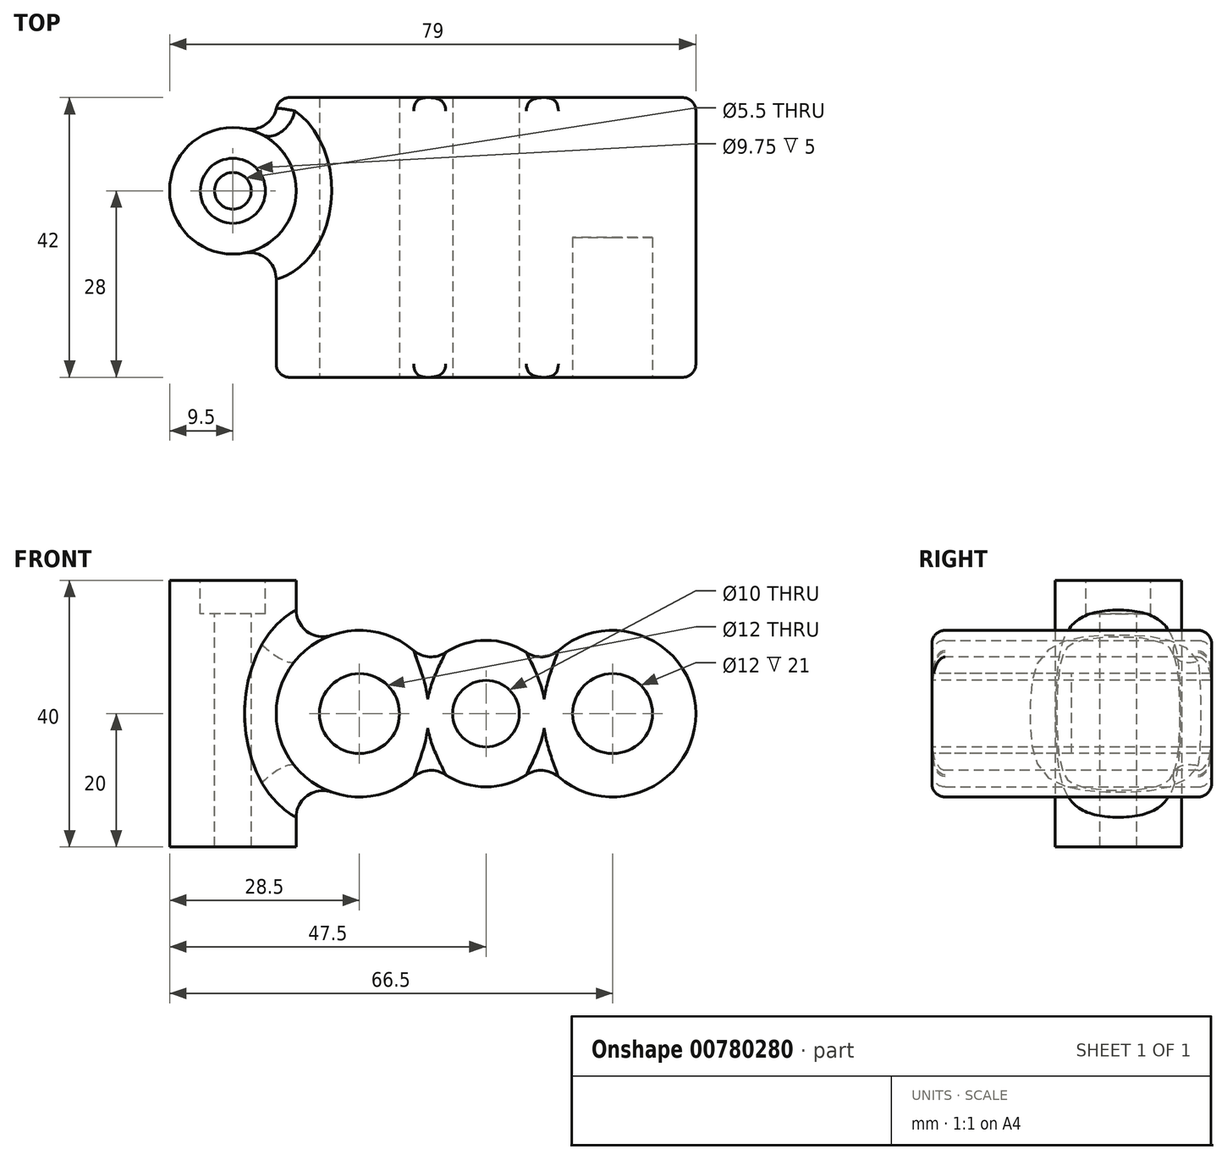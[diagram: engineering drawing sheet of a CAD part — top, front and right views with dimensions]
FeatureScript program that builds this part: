
annotation { "Feature Type Name" : "Feature", "Feature Type Description" : "" }
export const myFeature = defineFeature(function(context is Context, id is Id, definition is map)
    precondition{}
    {
        {
            var Q0;
            Q0=qCreatedBy(makeId("Front.planeOp"),FACE);
            var sketch = newSketch(context, id + "F0", { "sketchPlane" : qUnion([Q0])});
            skArc(sketch, "E0", {"start": v(10.43, 6.9) * mm, "mid": v(-12.5, 0) * mm, "end": v(10.43, -6.9) * mm});
            skArc(sketch, "E1", {"start": v(27.57, 6.9) * mm, "mid": v(19, 11) * mm, "end": v(10.43, 6.9) * mm});
            skArc(sketch, "E2", {"start": v(27.57, -6.9) * mm, "mid": v(50.5, 0) * mm, "end": v(27.57, 6.9) * mm});
            skArc(sketch, "E3.trimOffspring", {"start": v(10.43, -6.9) * mm, "mid": v(19, -11) * mm, "end": v(27.57, -6.9) * mm});
            skSolve(sketch);
        }
        {
            var Q0;
            Q0 = qSketchRegion(id + "F0", true);
            extrude(context, id + "F1", {"entities" : qUnion([Q0]), "depth" : 42 * mm, "offsetDistance" : 25 * mm});
        }
        {
            var Q0;
            Q0=makeQuery(id+"F1.opExtrude","CAP_FACE",FACE,{"disambiguationData":[OSD([sQuery(id+"F0.wireOp",EDGE,"E0"),sQuery(id+"F0.wireOp",EDGE,"E1"),sQuery(id+"F0.wireOp",EDGE,"E2"),sQuery(id+"F0.wireOp",EDGE,"E3.trimOffspring")])],"isStart":false});
            var sketch = newSketch(context, id + "F2", { "sketchPlane" : qUnion([Q0])});
            skCircle(sketch, "E4", {"center": v(0, 0) * mm, "radius": 6 * mm});
            skCircle(sketch, "E5", {"center": v(19, 0) * mm, "radius": 5 * mm});
            skSolve(sketch);
        }
        {
            var Q0;
            Q0 = qSketchRegion(id + "F2", true);
            extrude(context, id + "F3", {"entities" : qUnion([Q0]), "operationType" : NewBodyOperationType.REMOVE, "endBound" : BoundingType.THROUGH_ALL, "oppositeDirection" : true, "depth" : 25 * mm, "offsetDistance" : 25 * mm});
        }
        {
            var Q0;
            Q0=makeQuery(id+"F1.opExtrude","CAP_FACE",FACE,{"disambiguationData":[OSD([sQuery(id+"F0.wireOp",EDGE,"E0"),sQuery(id+"F0.wireOp",EDGE,"E1"),sQuery(id+"F0.wireOp",EDGE,"E2"),sQuery(id+"F0.wireOp",EDGE,"E3.trimOffspring")])],"isStart":false});
            var sketch = newSketch(context, id + "F4", { "sketchPlane" : qUnion([Q0])});
            skCircle(sketch, "E6", {"center": v(38, 0) * mm, "radius": 6 * mm});
            skSolve(sketch);
        }
        {
            var Q0;
            Q0 = qSketchRegion(id + "F4", true);
            extrude(context, id + "F5", {"entities" : qUnion([Q0]), "operationType" : NewBodyOperationType.REMOVE, "oppositeDirection" : true, "depth" : 21 * mm, "offsetDistance" : 25 * mm});
        }
        {
            var Q0;
            Q0=makeQuery(id+"F1.opExtrude","CAP_EDGE",EDGE,{"disambiguationData":[OSD([sQuery(id+"F0.wireOp",EDGE,"E0")])],"isStart":false});
            var Q1;
            Q1=makeQuery(id+"F1.opExtrude","CAP_EDGE",EDGE,{"disambiguationData":[OSD([sQuery(id+"F0.wireOp",EDGE,"E1")])],"isStart":false});
            var Q2;
            Q2=makeQuery(id+"F1.opExtrude","CAP_EDGE",EDGE,{"disambiguationData":[OSD([sQuery(id+"F0.wireOp",EDGE,"E2")])],"isStart":false});
            var Q3;
            Q3=makeQuery(id+"F1.opExtrude","CAP_EDGE",EDGE,{"disambiguationData":[OSD([sQuery(id+"F0.wireOp",EDGE,"E3.trimOffspring")])],"isStart":false});
            fillet(context, id + "F6", {"entities" : qUnion([Q0, Q1, Q2, Q3]), "radius" : 2 * mm, "tangentPropagation" : true, "allowEdgeOverflow" : false});
        }
        {
            var Q0;
            Q0=makeQuery(id+"F1.opExtrude","CAP_EDGE",EDGE,{"disambiguationData":[OSD([sQuery(id+"F0.wireOp",EDGE,"E2")])],"isStart":true});
            var Q1;
            Q1=makeQuery(id+"F1.opExtrude","CAP_EDGE",EDGE,{"disambiguationData":[OSD([sQuery(id+"F0.wireOp",EDGE,"E1")])],"isStart":true});
            var Q2;
            Q2=makeQuery(id+"F1.opExtrude","CAP_EDGE",EDGE,{"disambiguationData":[OSD([sQuery(id+"F0.wireOp",EDGE,"E0")])],"isStart":true});
            var Q3;
            Q3=makeQuery(id+"F1.opExtrude","CAP_EDGE",EDGE,{"disambiguationData":[OSD([sQuery(id+"F0.wireOp",EDGE,"E3.trimOffspring")])],"isStart":true});
            fillet(context, id + "F7", {"entities" : qUnion([Q0, Q1, Q2, Q3]), "radius" : 2 * mm, "tangentPropagation" : true, "allowEdgeOverflow" : false});
        }
        {
            var Q0;
            Q0=makeQuery(id+"F1.opExtrude","SWEPT_EDGE",EDGE,{"disambiguationData":[OSD([sQuery(id+"F0.wireOp",EDGE,"E0"),sQuery(id+"F0.wireOp",EDGE,"E1")])]});
            var Q1;
            Q1=makeQuery(id+"F1.opExtrude","SWEPT_EDGE",EDGE,{"disambiguationData":[OSD([sQuery(id+"F0.wireOp",EDGE,"E1"),sQuery(id+"F0.wireOp",EDGE,"E2")])]});
            var Q2;
            Q2=makeQuery(id+"F1.opExtrude","SWEPT_EDGE",EDGE,{"disambiguationData":[OSD([sQuery(id+"F0.wireOp",EDGE,"E0"),sQuery(id+"F0.wireOp",EDGE,"E3.trimOffspring")])]});
            var Q3;
            Q3=makeQuery(id+"F1.opExtrude","SWEPT_EDGE",EDGE,{"disambiguationData":[OSD([sQuery(id+"F0.wireOp",EDGE,"E2"),sQuery(id+"F0.wireOp",EDGE,"E3.trimOffspring")])]});
            fillet(context, id + "F8", {"entities" : qUnion([Q0, Q1, Q2, Q3]), "radius" : 4 * mm, "tangentPropagation" : true, "allowEdgeOverflow" : false});
        }
        {
            var Q0;
            Q0=qCreatedBy(makeId("Top.planeOp"),FACE);
            var sketch = newSketch(context, id + "F9", { "sketchPlane" : qUnion([Q0])});
            skCircle(sketch, "E7", {"center": v(-19, -14) * mm, "radius": 9.5 * mm});
            skSolve(sketch);
        }
        {
            var Q0;
            Q0 = qSketchRegion(id + "F9", true);
            extrude(context, id + "F10", {"entities" : qUnion([Q0]), "operationType" : NewBodyOperationType.ADD, "endBound" : BoundingType.SYMMETRIC, "depth" : 40 * mm, "offsetDistance" : 25 * mm});
        }
        {
            var Q0;
            Q0=makeQuery(id+"F10.opExtrude","CAP_FACE",FACE,{"disambiguationData":[OSD([sQuery(id+"F9.wireOp",EDGE,"E7")])],"isStart":false});
            var sketch = newSketch(context, id + "F11", { "sketchPlane" : qUnion([Q0])});
            skCircle(sketch, "E8", {"center": v(-19, -14) * mm, "radius": 9.5 * mm});
            skSolve(sketch);
        }
        {
            var Q0;
            Q0=sQuery(id+"F11.wireOp",VERTEX,"E8.center");
            var Q1;
            Q1=makeQuery(id+"F1.opExtrude","SWEPT_BODY",BODY,{"disambiguationData":[OSD([sQuery(id+"F0.wireOp",EDGE,"E0"),sQuery(id+"F0.wireOp",EDGE,"E1"),sQuery(id+"F0.wireOp",EDGE,"E2"),sQuery(id+"F0.wireOp",EDGE,"E3.trimOffspring")])]});
            hole(context, id + "F12", {"style" : HoleStyle.C_BORE, "endStyle" : HoleEndStyle.THROUGH, "standardTappedOrClearance" : lookupTablePath({ "standard" : "ISO", "fit" : "Normal", "size" : "M5", "type" : "Clearance" }), "standardBlindInLast" : lookupTablePath({ "fit" : "Standard", "standard" : "ISO", "size" : "M5", "type" : "Clearance" }), "holeDiameter" : 5.5 * mm, "cBoreDiameter" : 9.75 * mm, "cBoreDepth" : 5 * mm, "majorDiameter" : 5 * mm, "isTappedThrough" : true, "tappedDepth" : 12 * mm, "tapClearance" : 3, "startFromSketch" : true, "locations" : qUnion([Q0]), "scope" : qUnion([Q1])});
        }
        {
            var Q0;
            Q0=makeQuery(id+"F10.boolean.opBoolean","INTERSECT",EDGE,{"derivedFrom":[makeQuery(id+"F1.opExtrude","SWEPT_FACE",FACE,{"disambiguationData":[OSD([sQuery(id+"F0.wireOp",EDGE,"E0")])]}),makeQuery(id+"F10.opExtrude","SWEPT_FACE",FACE,{"disambiguationData":[OSD([sQuery(id+"F9.wireOp",EDGE,"E7")])]})]});
            fillet(context, id + "F13", {"entities" : qUnion([Q0]), "radius" : 4 * mm, "tangentPropagation" : true, "allowEdgeOverflow" : false});
        }
    });
